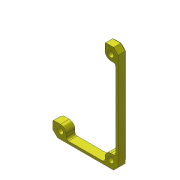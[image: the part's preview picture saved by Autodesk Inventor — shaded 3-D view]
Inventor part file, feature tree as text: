
AUTODESK INVENTOR PART (.ipt)
format: ipt  version: 2019.4 (Build 234330000, 330)  size: 200,704 bytes
history: native  units: mm
features: sketch x2, extrude x2, other x1, hole x1
ambient origin geometry x8: Origin, YZ Plane, XZ Plane, XY Plane, X Axis, Y Axis, Z Axis, Center Point
bodies: Body1 (feature_tree)
feature tree (6):
  other  "ソリッド1"
  sketch  "スケッチ1"
  extrude  "押し出し1"  Depth=2.0mm
  hole  "穴1"  [1 undecoded]
  extrude  "押し出し2"  Depth=2.0mm
  sketch  "スケッチ3"
note: 1 required parameter value undecoded (feature->parameter linkage not recoverable at this tier; creation-order binding heuristic only, values carry confidence <= 0.55)
